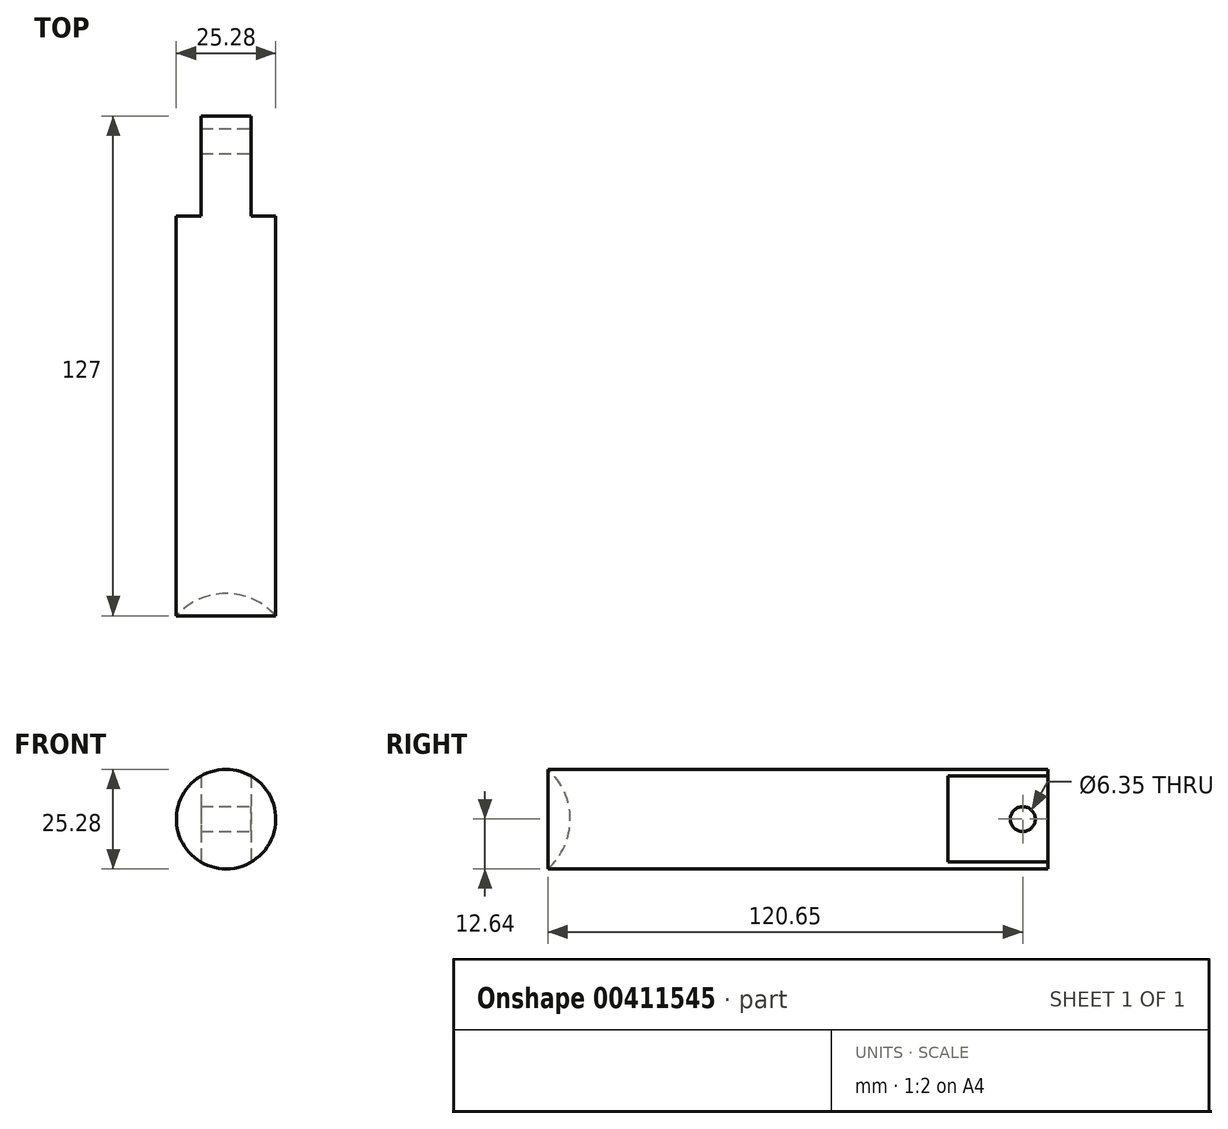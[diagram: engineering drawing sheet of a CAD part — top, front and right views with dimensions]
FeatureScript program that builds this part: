
annotation { "Feature Type Name" : "Feature", "Feature Type Description" : "" }
export const myFeature = defineFeature(function(context is Context, id is Id, definition is map)
    precondition{}
    {
        {
            var Q0;
            Q0=qCreatedBy(makeId("Front.planeOp"),FACE);
            var sketch = newSketch(context, id + "F0", { "sketchPlane" : qUnion([Q0])});
            skCircle(sketch, "E0", {"center": v(0, 0) * mm, "radius": 12.64 * mm});
            skSolve(sketch);
        }
        {
            var Q0;
            Q0=makeQuery(id+"F0.imprint","IMPRINT",FACE,{"disambiguationData":[TD([[makeQuery(id+"F0.imprint","IMPRINT",EDGE,{"derivedFrom":sQuery(id+"F0.wireOp",EDGE,"E0")}),1.0]])]});
            extrude(context, id + "F1", {"entities" : qUnion([Q0]), "depth" : 127 * mm});
        }
        {
            var Q0;
            Q0=qCreatedBy(makeId("Top.planeOp"),FACE);
            var sketch = newSketch(context, id + "F2", { "sketchPlane" : qUnion([Q0])});
            skLineSegment(sketch, "E1", {"start": v(6.35, 10.47) * mm, "end": v(6.35, -25.4) * mm});
            skLineSegment(sketch, "E2", {"start": v(6.35, -25.4) * mm, "end": v(27.52, -25.4) * mm});
            skLineSegment(sketch, "E3", {"start": v(27.52, -25.4) * mm, "end": v(27.52, 10.47) * mm});
            skLineSegment(sketch, "E4", {"start": v(27.52, 10.47) * mm, "end": v(6.35, 10.47) * mm});
            skLineSegment(sketch, "E5", {"start": v(0, 43.64) * mm, "end": v(0, 10.15) * mm, "construction": true});
            skLineSegment(sketch, "E6.MirrorCS", {"start": v(-6.35, -25.4) * mm, "end": v(-27.52, -25.4) * mm});
            skLineSegment(sketch, "E7.MirrorCS", {"start": v(-27.52, -25.4) * mm, "end": v(-27.52, 10.47) * mm});
            skLineSegment(sketch, "E8.MirrorCS", {"start": v(-6.35, 10.47) * mm, "end": v(-6.35, -25.4) * mm});
            skLineSegment(sketch, "E9.MirrorCS", {"start": v(-27.52, 10.47) * mm, "end": v(-6.35, 10.47) * mm});
            skSolve(sketch);
        }
        {
            var Q0;
            Q0=makeQuery(id+"F2.imprint","IMPRINT",FACE,{"disambiguationData":[TD([[makeQuery(id+"F2.imprint","IMPRINT",EDGE,{"derivedFrom":sQuery(id+"F2.wireOp",EDGE,"E1")}),1.0]])]});
            var Q1;
            Q1=makeQuery(id+"F2.imprint","IMPRINT",FACE,{"disambiguationData":[TD([[makeQuery(id+"F2.imprint","IMPRINT",EDGE,{"derivedFrom":sQuery(id+"F2.wireOp",EDGE,"E7.MirrorCS")}),-1.0]])]});
            extrude(context, id + "F3", {"entities" : qUnion([Q0, Q1]), "operationType" : NewBodyOperationType.REMOVE, "oppositeDirection" : true, "depth" : 50.8 * mm, "symmetric" : true});
        }
        {
            var Q0;
            Q0=qCreatedBy(makeId("Top.planeOp"),FACE);
            var sketch = newSketch(context, id + "F4", { "sketchPlane" : qUnion([Q0])});
            skArc(sketch, "E10", {"start": v(16.9, -138.22) * mm, "mid": v(0, -121.32) * mm, "end": v(-16.9, -138.22) * mm});
            skLineSegment(sketch, "E11", {"start": v(-12.64, -127) * mm, "end": v(-12.64, -25.4) * mm});
            skLineSegment(sketch, "E12", {"start": v(12.64, -25.4) * mm, "end": v(12.64, -127) * mm});
            skLineSegment(sketch, "E13", {"start": v(0, -138.22) * mm, "end": v(19.38, -138.22) * mm, "construction": true});
            skLineSegment(sketch, "E14", {"start": v(16.9, -138.22) * mm, "end": v(-16.9, -138.22) * mm});
            skSolve(sketch);
        }
        {
            var Q0;
            {var subQ0=sQuery(id+"F4.wireOp",EDGE,"E14");Q0=makeQuery(id+"F4.imprint","IMPRINT",FACE,{"disambiguationData":[TD([[makeQuery(id+"F4.imprint","IMPRINT",EDGE,{"derivedFrom":subQ0}),-1.0]])]});}
            var Q1;
            Q1=sQuery(id+"F4.wireOp",EDGE,"E13");
            revolve(context, id + "F5", {"operationType" : NewBodyOperationType.REMOVE, "entities" : qUnion([Q0]), "axis" : qUnion([Q1]), "revolveType" : RevolveType.FULL, "oppositeDirection" : true});
        }
        {
            var Q0;
            Q0=makeQuery(id+"F3.boolean.opBoolean","COPY",FACE,{"derivedFrom":makeQuery(id+"F3.opExtrude","SWEPT_FACE",FACE,{"disambiguationData":[OSD([sQuery(id+"F2.wireOp",EDGE,"E1")])]})});
            var sketch = newSketch(context, id + "F6", { "sketchPlane" : qUnion([Q0])});
            skCircle(sketch, "E15", {"center": v(-6.35, 0) * mm, "radius": 3.18 * mm});
            skSolve(sketch);
        }
        {
            var Q0;
            Q0=makeQuery(id+"F6.imprint","IMPRINT",FACE,{"disambiguationData":[TD([[makeQuery(id+"F6.imprint","IMPRINT",EDGE,{"derivedFrom":sQuery(id+"F6.wireOp",EDGE,"E15")}),1.0]])]});
            extrude(context, id + "F7", {"entities" : qUnion([Q0]), "operationType" : NewBodyOperationType.REMOVE, "endBound" : BoundingType.THROUGH_ALL, "oppositeDirection" : true, "depth" : 25.4 * mm});
        }
    });
